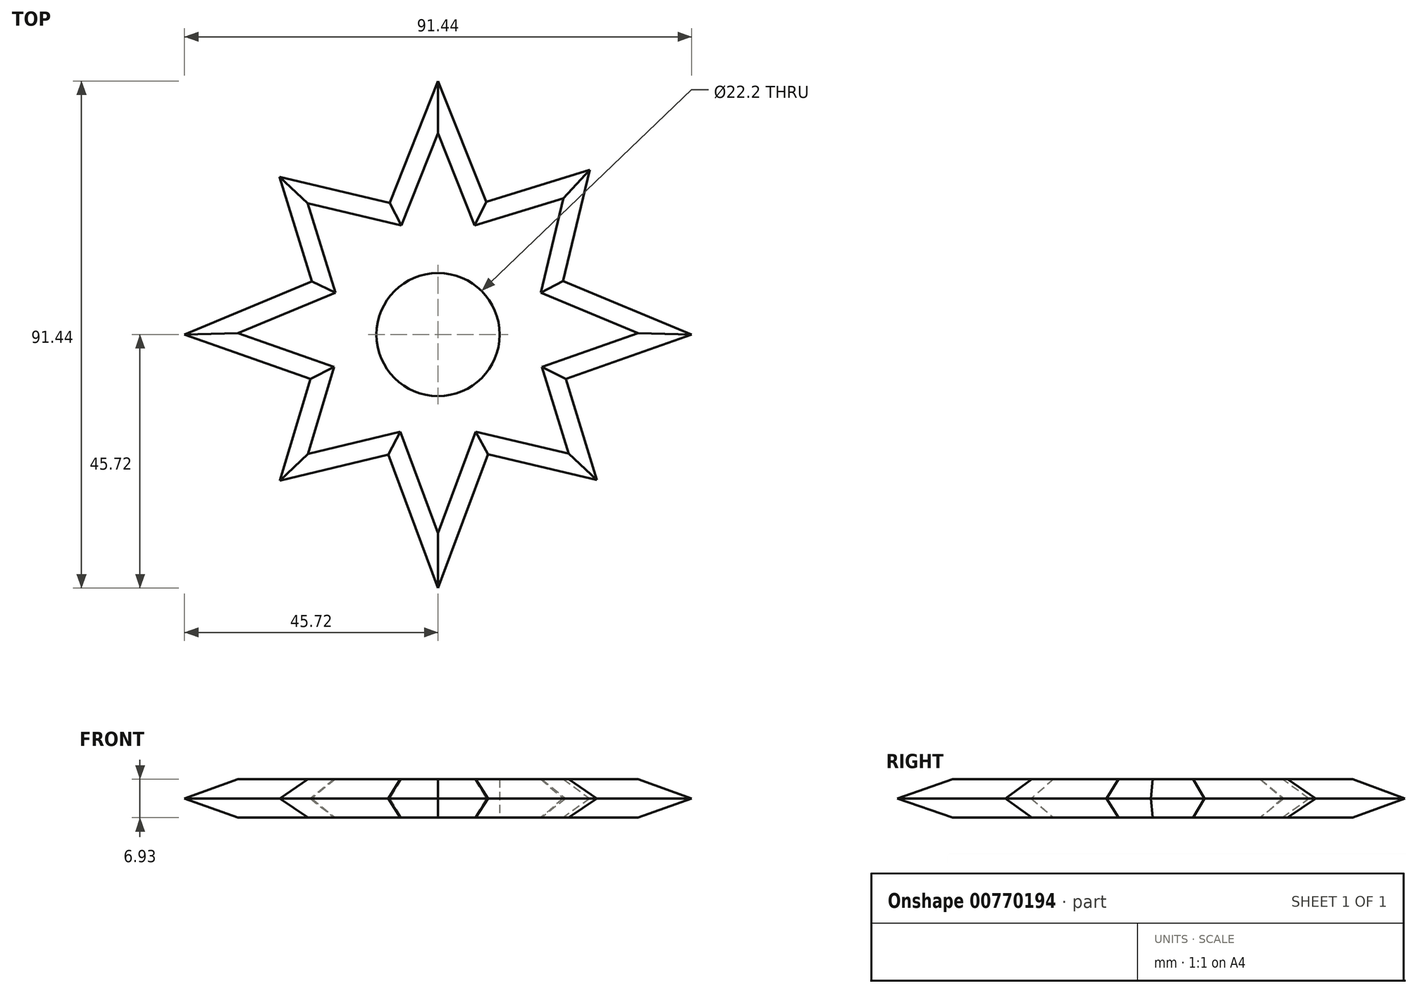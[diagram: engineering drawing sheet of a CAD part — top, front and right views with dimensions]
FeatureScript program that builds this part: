
annotation { "Feature Type Name" : "Feature", "Feature Type Description" : "" }
export const myFeature = defineFeature(function(context is Context, id is Id, definition is map)
    precondition{}
    {
        {
            var Q0;
            Q0=qCreatedBy(makeId("Top.planeOp"),FACE);
            var sketch = newSketch(context, id + "F0", { "sketchPlane" : qUnion([Q0])});
            skCircle(sketch, "E0", {"center": v(0, 0) * mm, "radius": 11.1 * mm});
            skLineSegment(sketch, "E1", {"start": v(0, 45.72) * mm, "end": v(-12.7, 13.75) * mm});
            skLineSegment(sketch, "E2", {"start": v(-12.7, 13.75) * mm, "end": v(-45.72, 0) * mm});
            skLineSegment(sketch, "E3", {"start": v(-45.72, 0) * mm, "end": v(-12.7, -11.65) * mm});
            skLineSegment(sketch, "E4", {"start": v(-12.7, -11.65) * mm, "end": v(0, -45.72) * mm});
            skLineSegment(sketch, "E5", {"start": v(0, -45.72) * mm, "end": v(12.7, -11.65) * mm});
            skLineSegment(sketch, "E6", {"start": v(12.7, -11.65) * mm, "end": v(45.72, 0) * mm});
            skLineSegment(sketch, "E7", {"start": v(45.72, 0) * mm, "end": v(12.7, 13.75) * mm});
            skLineSegment(sketch, "E8", {"start": v(12.7, 13.75) * mm, "end": v(0, 45.72) * mm});
            skSolve(sketch);
        }
        {
            var Q0;
            Q0=makeQuery(id+"F0.imprint","IMPRINT",FACE,{"disambiguationData":[TD([[makeQuery(id+"F0.imprint","IMPRINT",EDGE,{"derivedFrom":sQuery(id+"F0.wireOp",EDGE,"E0")}),-1.0]])]});
            extrude(context, id + "F1", {"entities" : qUnion([Q0]), "depth" : 6.93 * mm, "offsetDistance" : 25.4 * mm});
        }
        {
            var Q0;
            Q0=makeQuery(id+"F1.opExtrude","CAP_EDGE",EDGE,{"disambiguationData":[OSD([sQuery(id+"F0.wireOp",EDGE,"E5")])],"isStart":false});
            var Q1;
            Q1=makeQuery(id+"F1.opExtrude","CAP_EDGE",EDGE,{"disambiguationData":[OSD([sQuery(id+"F0.wireOp",EDGE,"E6")])],"isStart":false});
            var Q2;
            Q2=makeQuery(id+"F1.opExtrude","CAP_EDGE",EDGE,{"disambiguationData":[OSD([sQuery(id+"F0.wireOp",EDGE,"E3")])],"isStart":false});
            var Q3;
            Q3=makeQuery(id+"F1.opExtrude","CAP_EDGE",EDGE,{"disambiguationData":[OSD([sQuery(id+"F0.wireOp",EDGE,"E1")])],"isStart":false});
            var Q4;
            Q4=makeQuery(id+"F1.opExtrude","CAP_EDGE",EDGE,{"disambiguationData":[OSD([sQuery(id+"F0.wireOp",EDGE,"E2")])],"isStart":false});
            var Q5;
            Q5=makeQuery(id+"F1.opExtrude","CAP_EDGE",EDGE,{"disambiguationData":[OSD([sQuery(id+"F0.wireOp",EDGE,"E8")])],"isStart":false});
            var Q6;
            Q6=makeQuery(id+"F1.opExtrude","CAP_EDGE",EDGE,{"disambiguationData":[OSD([sQuery(id+"F0.wireOp",EDGE,"E7")])],"isStart":false});
            var Q7;
            Q7=makeQuery(id+"F1.opExtrude","CAP_EDGE",EDGE,{"disambiguationData":[OSD([sQuery(id+"F0.wireOp",EDGE,"E4")])],"isStart":false});
            chamfer(context, id + "F2", {"entities" : qUnion([Q0, Q1, Q2, Q3, Q4, Q5, Q6, Q7]), "width" : 3.47 * mm, "tangentPropagation" : true});
        }
        {
            var Q0;
            Q0=makeQuery(id+"F1.opExtrude","CAP_EDGE",EDGE,{"disambiguationData":[OSD([sQuery(id+"F0.wireOp",EDGE,"E5")])],"isStart":true});
            var Q1;
            Q1=makeQuery(id+"F1.opExtrude","CAP_EDGE",EDGE,{"disambiguationData":[OSD([sQuery(id+"F0.wireOp",EDGE,"E6")])],"isStart":true});
            var Q2;
            Q2=makeQuery(id+"F1.opExtrude","CAP_EDGE",EDGE,{"disambiguationData":[OSD([sQuery(id+"F0.wireOp",EDGE,"E3")])],"isStart":true});
            var Q3;
            Q3=makeQuery(id+"F1.opExtrude","CAP_EDGE",EDGE,{"disambiguationData":[OSD([sQuery(id+"F0.wireOp",EDGE,"E4")])],"isStart":true});
            var Q4;
            Q4=makeQuery(id+"F1.opExtrude","CAP_EDGE",EDGE,{"disambiguationData":[OSD([sQuery(id+"F0.wireOp",EDGE,"E8")])],"isStart":true});
            var Q5;
            Q5=makeQuery(id+"F1.opExtrude","CAP_EDGE",EDGE,{"disambiguationData":[OSD([sQuery(id+"F0.wireOp",EDGE,"E7")])],"isStart":true});
            var Q6;
            Q6=makeQuery(id+"F1.opExtrude","CAP_EDGE",EDGE,{"disambiguationData":[OSD([sQuery(id+"F0.wireOp",EDGE,"E2")])],"isStart":true});
            var Q7;
            Q7=makeQuery(id+"F1.opExtrude","CAP_EDGE",EDGE,{"disambiguationData":[OSD([sQuery(id+"F0.wireOp",EDGE,"E1")])],"isStart":true});
            chamfer(context, id + "F3", {"entities" : qUnion([Q0, Q1, Q2, Q3, Q4, Q5, Q6, Q7]), "width" : 3.47 * mm, "tangentPropagation" : true});
        }
        {
            var Q0;
            Q0=makeQuery(id+"F1.opExtrude","CAP_FACE",FACE,{"disambiguationData":[OSD([sQuery(id+"F0.wireOp",EDGE,"E0"),sQuery(id+"F0.wireOp",EDGE,"E1"),sQuery(id+"F0.wireOp",EDGE,"E2"),sQuery(id+"F0.wireOp",EDGE,"E3"),sQuery(id+"F0.wireOp",EDGE,"E4"),sQuery(id+"F0.wireOp",EDGE,"E5"),sQuery(id+"F0.wireOp",EDGE,"E6"),sQuery(id+"F0.wireOp",EDGE,"E7"),sQuery(id+"F0.wireOp",EDGE,"E8")])],"isStart":false});
            var sketch = newSketch(context, id + "F4", { "sketchPlane" : qUnion([Q0])});
            skPoint(sketch, "E9", {"position": v(-10.02, 11.11) * mm});
            skPoint(sketch, "E10", {"position": v(10.02, 11.11) * mm});
            skPoint(sketch, "E11", {"position": v(10.02, -8.92) * mm});
            skPoint(sketch, "E12", {"position": v(-10.02, -8.92) * mm});
            skLineSegment(sketch, "E13", {"start": v(-21.74, 6.23) * mm, "end": v(-28.6, 28.43) * mm});
            skLineSegment(sketch, "E14", {"start": v(-21.74, 6.23) * mm, "end": v(-10.02, 11.11) * mm});
            skLineSegment(sketch, "E15", {"start": v(-10.02, 11.11) * mm, "end": v(-28.6, 28.43) * mm});
            skLineSegment(sketch, "E16", {"start": v(10.02, 11.11) * mm, "end": v(27.34, 29.7) * mm});
            skLineSegment(sketch, "E17", {"start": v(10.02, -8.92) * mm, "end": v(28.6, -26.24) * mm});
            skLineSegment(sketch, "E18", {"start": v(-10.02, -8.92) * mm, "end": v(-28.5, -26.33) * mm});
            skLineSegment(sketch, "E19", {"start": v(-10.02, 11.11) * mm, "end": v(-5.33, 22.92) * mm});
            skLineSegment(sketch, "E20", {"start": v(-5.33, 22.92) * mm, "end": v(-28.6, 28.43) * mm});
            skLineSegment(sketch, "E21", {"start": v(10.02, 11.11) * mm, "end": v(5.33, 22.92) * mm});
            skLineSegment(sketch, "E22", {"start": v(5.33, 22.92) * mm, "end": v(27.34, 29.7) * mm});
            skLineSegment(sketch, "E23", {"start": v(10.02, 11.11) * mm, "end": v(21.74, 6.23) * mm});
            skLineSegment(sketch, "E24", {"start": v(21.74, 6.23) * mm, "end": v(27.34, 29.7) * mm});
            skLineSegment(sketch, "E25", {"start": v(-10.02, -8.92) * mm, "end": v(-22, -4.7) * mm});
            skLineSegment(sketch, "E26", {"start": v(-22, -4.7) * mm, "end": v(-28.5, -26.33) * mm});
            skLineSegment(sketch, "E27", {"start": v(-10.02, -8.92) * mm, "end": v(-5.58, -20.82) * mm});
            skLineSegment(sketch, "E28", {"start": v(-5.58, -20.82) * mm, "end": v(-28.5, -26.33) * mm});
            skLineSegment(sketch, "E29", {"start": v(10.02, -8.92) * mm, "end": v(5.58, -20.82) * mm});
            skLineSegment(sketch, "E30", {"start": v(5.58, -20.82) * mm, "end": v(28.6, -26.24) * mm});
            skLineSegment(sketch, "E31", {"start": v(10.02, -8.92) * mm, "end": v(22, -4.7) * mm});
            skLineSegment(sketch, "E32", {"start": v(22, -4.7) * mm, "end": v(28.6, -26.24) * mm});
            skSolve(sketch);
        }
        {
            var Q0;
            Q0=makeQuery(id+"F4.imprint","IMPRINT",FACE,{"disambiguationData":[TD([[makeQuery(id+"F4.imprint","IMPRINT",EDGE,{"derivedFrom":sQuery(id+"F4.wireOp",EDGE,"E15")}),-1.0]])]});
            var Q1;
            Q1=makeQuery(id+"F4.imprint","IMPRINT",FACE,{"disambiguationData":[TD([[makeQuery(id+"F4.imprint","IMPRINT",EDGE,{"derivedFrom":sQuery(id+"F4.wireOp",EDGE,"E13")}),-1.0]])]});
            var Q2;
            Q2=makeQuery(id+"F4.imprint","IMPRINT",FACE,{"disambiguationData":[TD([[makeQuery(id+"F4.imprint","IMPRINT",EDGE,{"derivedFrom":sQuery(id+"F4.wireOp",EDGE,"E16")}),1.0]])]});
            var Q3;
            Q3=makeQuery(id+"F4.imprint","IMPRINT",FACE,{"disambiguationData":[TD([[makeQuery(id+"F4.imprint","IMPRINT",EDGE,{"derivedFrom":sQuery(id+"F4.wireOp",EDGE,"E16")}),-1.0]])]});
            var Q4;
            Q4=makeQuery(id+"F4.imprint","IMPRINT",FACE,{"disambiguationData":[TD([[makeQuery(id+"F4.imprint","IMPRINT",EDGE,{"derivedFrom":sQuery(id+"F4.wireOp",EDGE,"E17")}),-1.0]])]});
            var Q5;
            Q5=makeQuery(id+"F4.imprint","IMPRINT",FACE,{"disambiguationData":[TD([[makeQuery(id+"F4.imprint","IMPRINT",EDGE,{"derivedFrom":sQuery(id+"F4.wireOp",EDGE,"E18")}),1.0]])]});
            var Q6;
            Q6=makeQuery(id+"F4.imprint","IMPRINT",FACE,{"disambiguationData":[TD([[makeQuery(id+"F4.imprint","IMPRINT",EDGE,{"derivedFrom":sQuery(id+"F4.wireOp",EDGE,"E18")}),-1.0]])]});
            var Q7;
            Q7=makeQuery(id+"F4.imprint","IMPRINT",FACE,{"disambiguationData":[TD([[makeQuery(id+"F4.imprint","IMPRINT",EDGE,{"derivedFrom":sQuery(id+"F4.wireOp",EDGE,"E17")}),1.0]])]});
            extrude(context, id + "F5", {"entities" : qUnion([Q0, Q1, Q2, Q3, Q4, Q5, Q6, Q7]), "operationType" : NewBodyOperationType.ADD, "oppositeDirection" : true, "depth" : 6.93 * mm, "offsetDistance" : 25.4 * mm});
        }
        {
            var Q0;
            Q0=makeQuery(id+"F5.opExtrude","CAP_EDGE",EDGE,{"disambiguationData":[OSD([sQuery(id+"F4.wireOp",EDGE,"E30")])],"isStart":true});
            var Q1;
            Q1=makeQuery(id+"F5.opExtrude","CAP_EDGE",EDGE,{"disambiguationData":[OSD([sQuery(id+"F4.wireOp",EDGE,"E32")])],"isStart":true});
            var Q2;
            Q2=makeQuery(id+"F5.opExtrude","CAP_EDGE",EDGE,{"disambiguationData":[OSD([sQuery(id+"F4.wireOp",EDGE,"E24")])],"isStart":true});
            var Q3;
            Q3=makeQuery(id+"F5.opExtrude","CAP_EDGE",EDGE,{"disambiguationData":[OSD([sQuery(id+"F4.wireOp",EDGE,"E28")])],"isStart":true});
            var Q4;
            Q4=makeQuery(id+"F5.opExtrude","CAP_EDGE",EDGE,{"disambiguationData":[OSD([sQuery(id+"F4.wireOp",EDGE,"E26")])],"isStart":true});
            var Q5;
            Q5=makeQuery(id+"F5.opExtrude","CAP_EDGE",EDGE,{"disambiguationData":[OSD([sQuery(id+"F4.wireOp",EDGE,"E13")])],"isStart":true});
            var Q6;
            Q6=makeQuery(id+"F5.opExtrude","CAP_EDGE",EDGE,{"disambiguationData":[OSD([sQuery(id+"F4.wireOp",EDGE,"E20")])],"isStart":true});
            var Q7;
            Q7=makeQuery(id+"F5.opExtrude","CAP_EDGE",EDGE,{"disambiguationData":[OSD([sQuery(id+"F4.wireOp",EDGE,"E22")])],"isStart":true});
            var Q8;
            Q8=makeQuery(id+"F5.opExtrude","CAP_EDGE",EDGE,{"disambiguationData":[OSD([sQuery(id+"F4.wireOp",EDGE,"E24")])],"isStart":false});
            var Q9;
            Q9=makeQuery(id+"F5.opExtrude","CAP_EDGE",EDGE,{"disambiguationData":[OSD([sQuery(id+"F4.wireOp",EDGE,"E32")])],"isStart":false});
            var Q10;
            Q10=makeQuery(id+"F5.opExtrude","CAP_EDGE",EDGE,{"disambiguationData":[OSD([sQuery(id+"F4.wireOp",EDGE,"E30")])],"isStart":false});
            var Q11;
            Q11=makeQuery(id+"F5.opExtrude","CAP_EDGE",EDGE,{"disambiguationData":[OSD([sQuery(id+"F4.wireOp",EDGE,"E28")])],"isStart":false});
            var Q12;
            Q12=makeQuery(id+"F5.opExtrude","CAP_EDGE",EDGE,{"disambiguationData":[OSD([sQuery(id+"F4.wireOp",EDGE,"E22")])],"isStart":false});
            var Q13;
            Q13=makeQuery(id+"F5.opExtrude","CAP_EDGE",EDGE,{"disambiguationData":[OSD([sQuery(id+"F4.wireOp",EDGE,"E20")])],"isStart":false});
            var Q14;
            Q14=makeQuery(id+"F5.opExtrude","CAP_EDGE",EDGE,{"disambiguationData":[OSD([sQuery(id+"F4.wireOp",EDGE,"E13")])],"isStart":false});
            var Q15;
            Q15=makeQuery(id+"F5.opExtrude","CAP_EDGE",EDGE,{"disambiguationData":[OSD([sQuery(id+"F4.wireOp",EDGE,"E26")])],"isStart":false});
            chamfer(context, id + "F6", {"entities" : qUnion([Q0, Q1, Q2, Q3, Q4, Q5, Q6, Q7, Q8, Q9, Q10, Q11, Q12, Q13, Q14, Q15]), "width" : 3.47 * mm, "tangentPropagation" : true});
        }
    });
